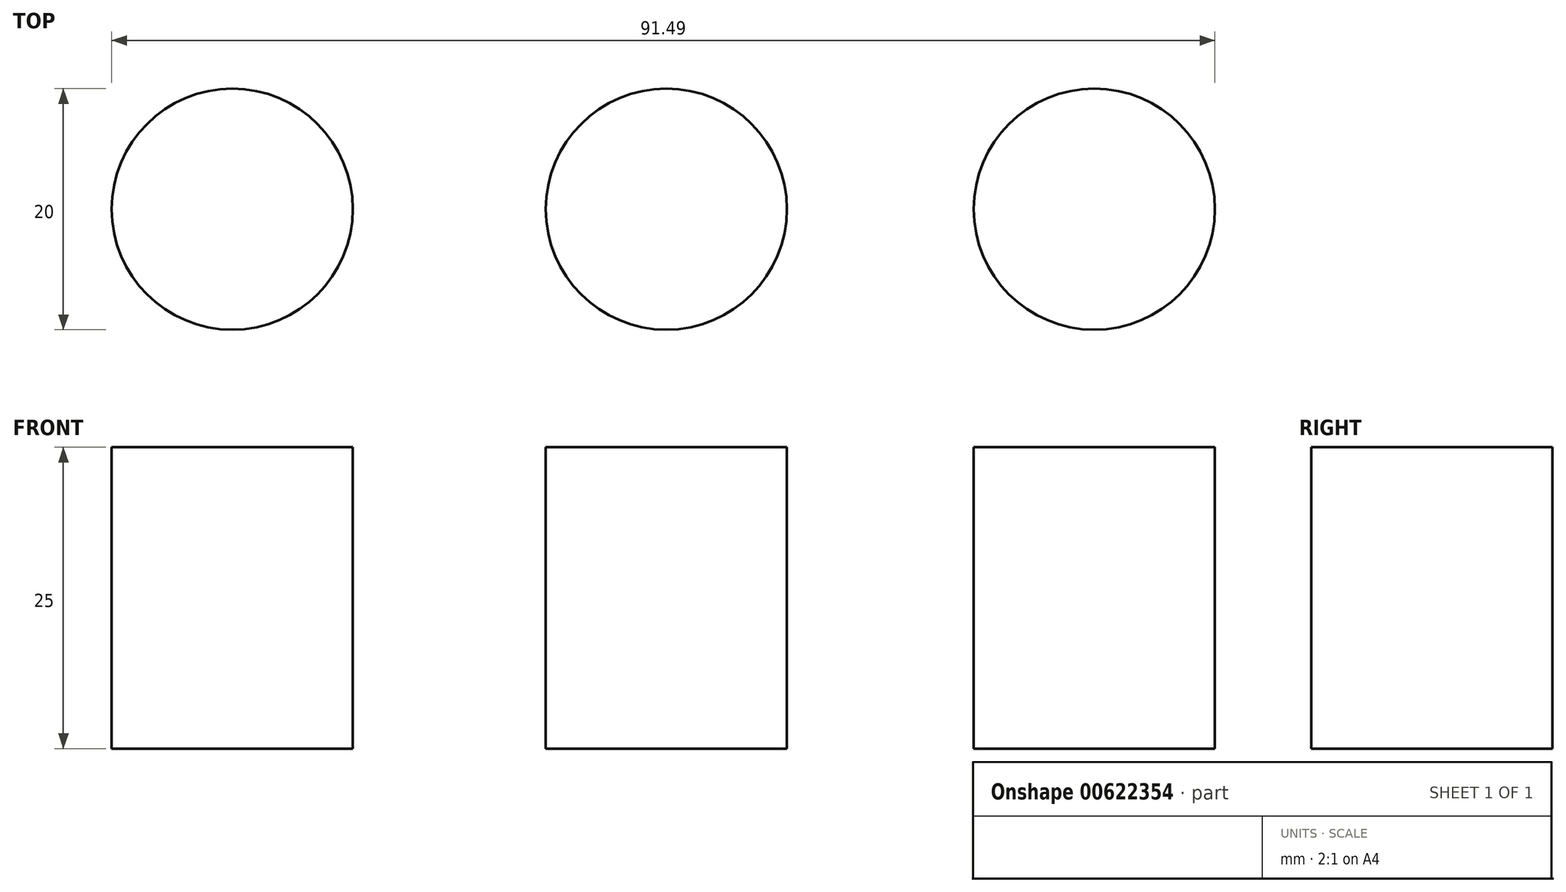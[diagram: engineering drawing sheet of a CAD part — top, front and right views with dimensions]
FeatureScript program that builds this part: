
annotation { "Feature Type Name" : "Feature", "Feature Type Description" : "" }
export const myFeature = defineFeature(function(context is Context, id is Id, definition is map)
    precondition{}
    {
        {
            var Q0;
            Q0=qCreatedBy(makeId("Top.planeOp"),FACE);
            var sketch = newSketch(context, id + "F0", { "sketchPlane" : qUnion([Q0])});
            skLineSegment(sketch, "E0.bottom", {"start": v(70, -30) * mm, "end": v(-70, -30) * mm});
            skLineSegment(sketch, "E0.top", {"start": v(70, 30) * mm, "end": v(-70, 30) * mm});
            skLineSegment(sketch, "E0.left", {"start": v(70, -30) * mm, "end": v(70, 30) * mm});
            skLineSegment(sketch, "E0.right", {"start": v(-70, -30) * mm, "end": v(-70, 30) * mm});
            skPoint(sketch, "E0.middle", {"position": v(0, 0) * mm});
            skSolve(sketch);
        }
        {
            var Q0;
            Q0 = qSketchRegion(id + "F0", true);
            extrude(context, id + "F1", {"entities" : qUnion([Q0]), "depth" : 25 * mm, "offsetDistance" : 25 * mm});
        }
        {
            var Q0;
            Q0=makeQuery(id+"F1.opExtrude","CAP_FACE",FACE,{"disambiguationData":[OSD([sQuery(id+"F0.wireOp",EDGE,"E0.bottom"),sQuery(id+"F0.wireOp",EDGE,"E0.top"),sQuery(id+"F0.wireOp",EDGE,"E0.left"),sQuery(id+"F0.wireOp",EDGE,"E0.right")])],"isStart":false});
            var sketch = newSketch(context, id + "F2", { "sketchPlane" : qUnion([Q0])});
            skLineSegment(sketch, "E1", {"start": v(-70, 0) * mm, "end": v(-49.23, 0) * mm});
            skPoint(sketch, "E1.endSnap0", {"position": v(-70, 0) * mm});
            skCircle(sketch, "E2", {"center": v(-36, 0) * mm, "radius": 10 * mm});
            skCircle(sketch, "E3", {"center": v(0, 0) * mm, "radius": 10 * mm});
            skCircle(sketch, "E4", {"center": v(35.5, 0) * mm, "radius": 10 * mm});
            skSolve(sketch);
        }
        {
            var Q0;
            Q0=makeQuery(id+"F2.imprint","IMPRINT",FACE,{"disambiguationData":[TD([[makeQuery(id+"F2.imprint","IMPRINT",EDGE,{"derivedFrom":sQuery(id+"F2.wireOp",EDGE,"E2")}),-1.0]])]});
            extrude(context, id + "F3", {"entities" : qUnion([Q0]), "operationType" : NewBodyOperationType.REMOVE, "oppositeDirection" : true, "depth" : 25 * mm, "offsetDistance" : 25 * mm});
        }
    });
